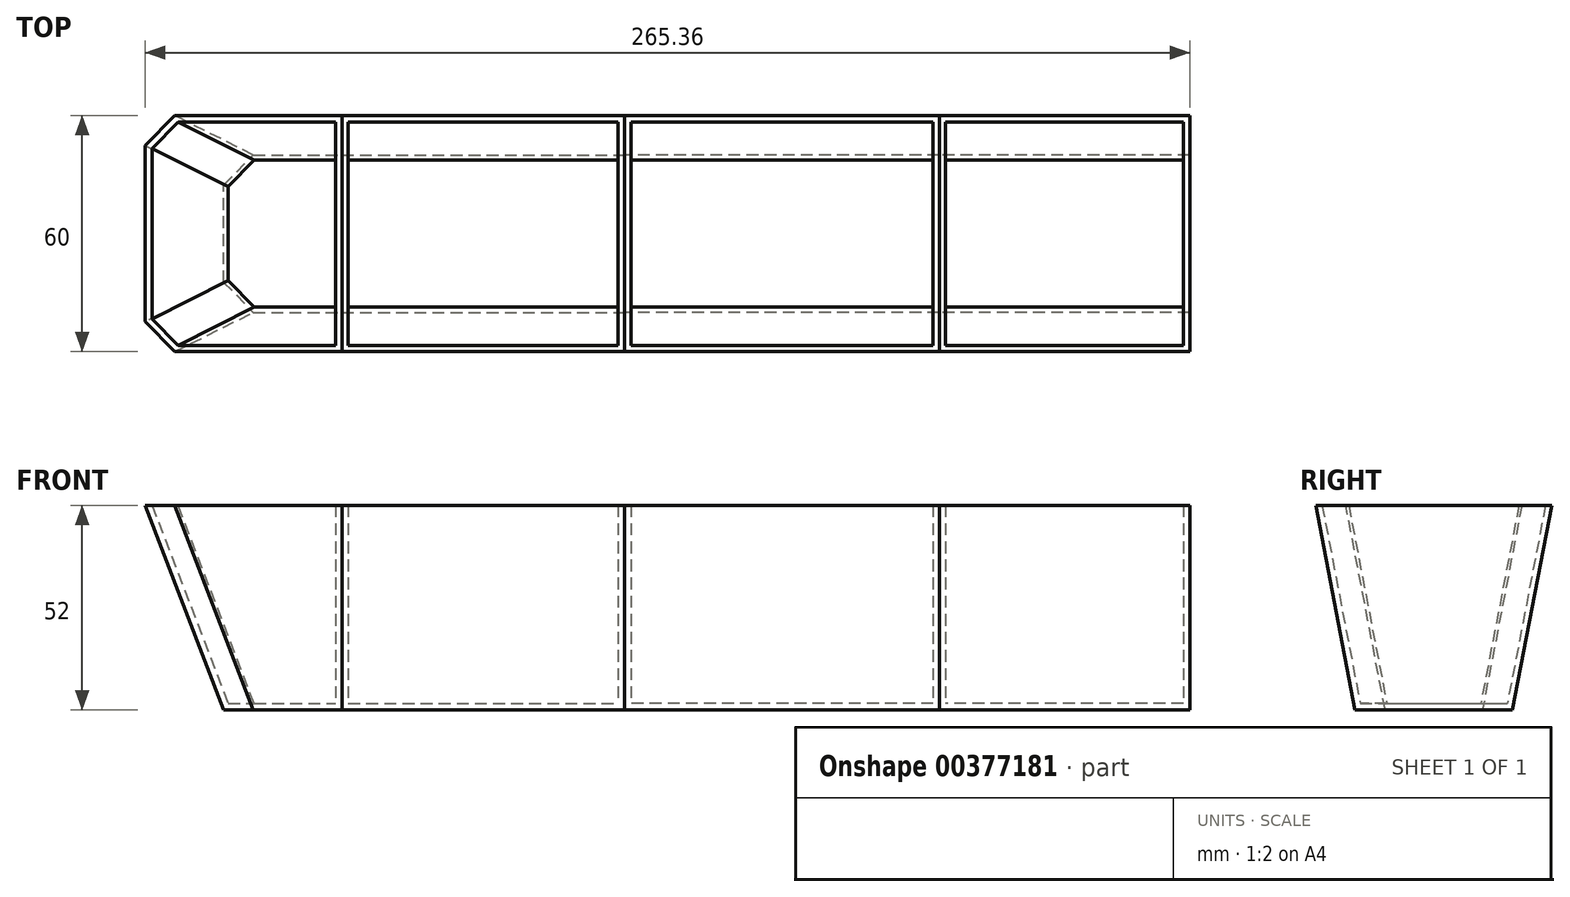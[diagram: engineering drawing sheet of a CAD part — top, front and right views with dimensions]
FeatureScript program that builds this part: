
annotation { "Feature Type Name" : "Feature", "Feature Type Description" : "" }
export const myFeature = defineFeature(function(context is Context, id is Id, definition is map)
    precondition{}
    {
        {
            var Q0;
            Q0=qCreatedBy(makeId("Right.planeOp"),FACE);
            var sketch = newSketch(context, id + "F0", { "sketchPlane" : qUnion([Q0])});
            skLineSegment(sketch, "E0", {"start": v(0, 0) * mm, "end": v(30, 0) * mm});
            skLineSegment(sketch, "E1", {"start": v(30, 0) * mm, "end": v(20, -52) * mm});
            skLineSegment(sketch, "E2", {"start": v(20, -52) * mm, "end": v(0, -52) * mm});
            skLineSegment(sketch, "E3.MirrorCS", {"start": v(0, 0) * mm, "end": v(-30, 0) * mm});
            skLineSegment(sketch, "E4.MirrorCS", {"start": v(-30, 0) * mm, "end": v(-20, -52) * mm});
            skLineSegment(sketch, "E5.MirrorCS", {"start": v(-20, -52) * mm, "end": v(0, -52) * mm});
            skSolve(sketch);
        }
        {
            var Q0;
            Q0=makeQuery(id+"F0.imprint","IMPRINT",FACE,{"disambiguationData":[TD([[makeQuery(id+"F0.imprint","IMPRINT",EDGE,{"derivedFrom":sQuery(id+"F0.wireOp",EDGE,"E0")}),-1.0]])]});
            extrude(context, id + "F1", {"entities" : qUnion([Q0]), "depth" : 80 * mm});
        }
        {
            var Q0;
            Q0=makeQuery(id+"F1.opExtrude","CAP_FACE",FACE,{"disambiguationData":[OSD([sQuery(id+"F0.wireOp",EDGE,"E0"),sQuery(id+"F0.wireOp",EDGE,"E1"),sQuery(id+"F0.wireOp",EDGE,"E2"),sQuery(id+"F0.wireOp",EDGE,"E3.MirrorCS"),sQuery(id+"F0.wireOp",EDGE,"E4.MirrorCS"),sQuery(id+"F0.wireOp",EDGE,"E5.MirrorCS")])],"isStart":false});
            var sketch = newSketch(context, id + "F2", { "sketchPlane" : qUnion([Q0])});
            skLineSegment(sketch, "E6.0.0", {"start": v(-30, 0) * mm, "end": v(-20, -52) * mm});
            skLineSegment(sketch, "E6.0.1", {"start": v(-20, -52) * mm, "end": v(20, -52) * mm});
            skLineSegment(sketch, "E6.0.2", {"start": v(20, -52) * mm, "end": v(30, 0) * mm});
            skLineSegment(sketch, "E6.0.3", {"start": v(30, 0) * mm, "end": v(-30, 0) * mm});
            skSolve(sketch);
        }
        {
            var Q0;
            Q0=makeQuery(id+"F1.opExtrude","CAP_FACE",FACE,{"disambiguationData":[OSD([sQuery(id+"F0.wireOp",EDGE,"E0"),sQuery(id+"F0.wireOp",EDGE,"E1"),sQuery(id+"F0.wireOp",EDGE,"E2"),sQuery(id+"F0.wireOp",EDGE,"E3.MirrorCS"),sQuery(id+"F0.wireOp",EDGE,"E4.MirrorCS"),sQuery(id+"F0.wireOp",EDGE,"E5.MirrorCS")])],"isStart":true});
            extrude(context, id + "F3", {"entities" : qUnion([Q0]), "depth" : 71.8 * mm});
        }
        {
            var Q0;
            Q0=makeQuery(id+"F3.opExtrude","CAP_FACE",FACE,{"disambiguationData":[OSD([sQuery(id+"F0.wireOp",EDGE,"E0"),sQuery(id+"F0.wireOp",EDGE,"E1"),sQuery(id+"F0.wireOp",EDGE,"E2"),sQuery(id+"F0.wireOp",EDGE,"E3.MirrorCS"),sQuery(id+"F0.wireOp",EDGE,"E4.MirrorCS"),sQuery(id+"F0.wireOp",EDGE,"E5.MirrorCS")])],"isStart":false});
            extrude(context, id + "F4", {"entities" : qUnion([Q0]), "depth" : 50 * mm});
        }
        {
            var Q0;
            Q0=makeQuery(id+"F4.opExtrude","CAP_EDGE",EDGE,{"disambiguationData":[OSD([sQuery(id+"F0.wireOp",EDGE,"E2"),sQuery(id+"F0.wireOp",EDGE,"E5.MirrorCS")])],"isStart":false});
            chamfer(context, id + "F5", {"entities" : qUnion([Q0]), "chamferType" : ChamferType.OFFSET_ANGLE, "width" : 20 * mm, "oppositeDirection" : false, "angle" : 69 * degree, "tangentPropagation" : true});
        }
        {
            var Q0;
            Q0=makeQuery(id+"F5.opChamfer","BLEND_EDGE",EDGE,{"blendedFrom":[makeQuery(id+"F4.opExtrude","CAP_EDGE",EDGE,{"disambiguationData":[OSD([sQuery(id+"F0.wireOp",EDGE,"E2"),sQuery(id+"F0.wireOp",EDGE,"E5.MirrorCS")])],"isStart":false}),makeQuery(id+"F4.opExtrude","SWEPT_FACE",FACE,{"disambiguationData":[OSD([sQuery(id+"F0.wireOp",EDGE,"E1")])]})],"blendedInto":[makeQuery(id+"F4.opExtrude","SWEPT_FACE",FACE,{"disambiguationData":[OSD([sQuery(id+"F0.wireOp",EDGE,"E1")])]})]});
            var Q1;
            Q1=makeQuery(id+"F5.opChamfer","BLEND_EDGE",EDGE,{"blendedFrom":[makeQuery(id+"F4.opExtrude","CAP_EDGE",EDGE,{"disambiguationData":[OSD([sQuery(id+"F0.wireOp",EDGE,"E2"),sQuery(id+"F0.wireOp",EDGE,"E5.MirrorCS")])],"isStart":false}),makeQuery(id+"F4.opExtrude","SWEPT_FACE",FACE,{"disambiguationData":[OSD([sQuery(id+"F0.wireOp",EDGE,"E4.MirrorCS")])]})],"blendedInto":[makeQuery(id+"F4.opExtrude","SWEPT_FACE",FACE,{"disambiguationData":[OSD([sQuery(id+"F0.wireOp",EDGE,"E4.MirrorCS")])]})]});
            chamfer(context, id + "F6", {"entities" : qUnion([Q0, Q1]), "chamferType" : ChamferType.OFFSET_ANGLE, "width" : 7 * mm, "oppositeDirection" : false, "angle" : 45 * degree, "tangentPropagation" : true});
        }
        {
            var Q0;
            Q0=makeQuery(id+"F1.opExtrude","SWEPT_FACE",FACE,{"disambiguationData":[OSD([sQuery(id+"F0.wireOp",EDGE,"E0"),sQuery(id+"F0.wireOp",EDGE,"E3.MirrorCS")])]});
            var Q1;
            Q1=makeQuery(id+"F3.opExtrude","SWEPT_FACE",FACE,{"disambiguationData":[OSD([sQuery(id+"F0.wireOp",EDGE,"E0"),sQuery(id+"F0.wireOp",EDGE,"E3.MirrorCS")])]});
            var Q2;
            Q2=makeQuery(id+"F4.opExtrude","SWEPT_FACE",FACE,{"disambiguationData":[OSD([sQuery(id+"F0.wireOp",EDGE,"E0"),sQuery(id+"F0.wireOp",EDGE,"E3.MirrorCS")])]});
            shell(context, id + "F7", {"entities" : qUnion([Q0, Q1, Q2]), "thickness" : 1.6 * mm});
        }
        {
            var Q0;
            Q0=makeQuery(id+"F2.imprint","IMPRINT",FACE,{"disambiguationData":[TD([[makeQuery(id+"F2.imprint","IMPRINT",EDGE,{"derivedFrom":sQuery(id+"F2.wireOp",EDGE,"E6.0.0")}),1.0]])]});
            extrude(context, id + "F8", {"entities" : qUnion([Q0]), "depth" : 63.6 * mm});
        }
        {
            var Q0;
            Q0=makeQuery(id+"F8.opExtrude","SWEPT_FACE",FACE,{"disambiguationData":[OSD([sQuery(id+"F2.wireOp",EDGE,"E6.0.3")])]});
            shell(context, id + "F9", {"entities" : qUnion([Q0]), "thickness" : 1.6 * mm});
        }
    });
